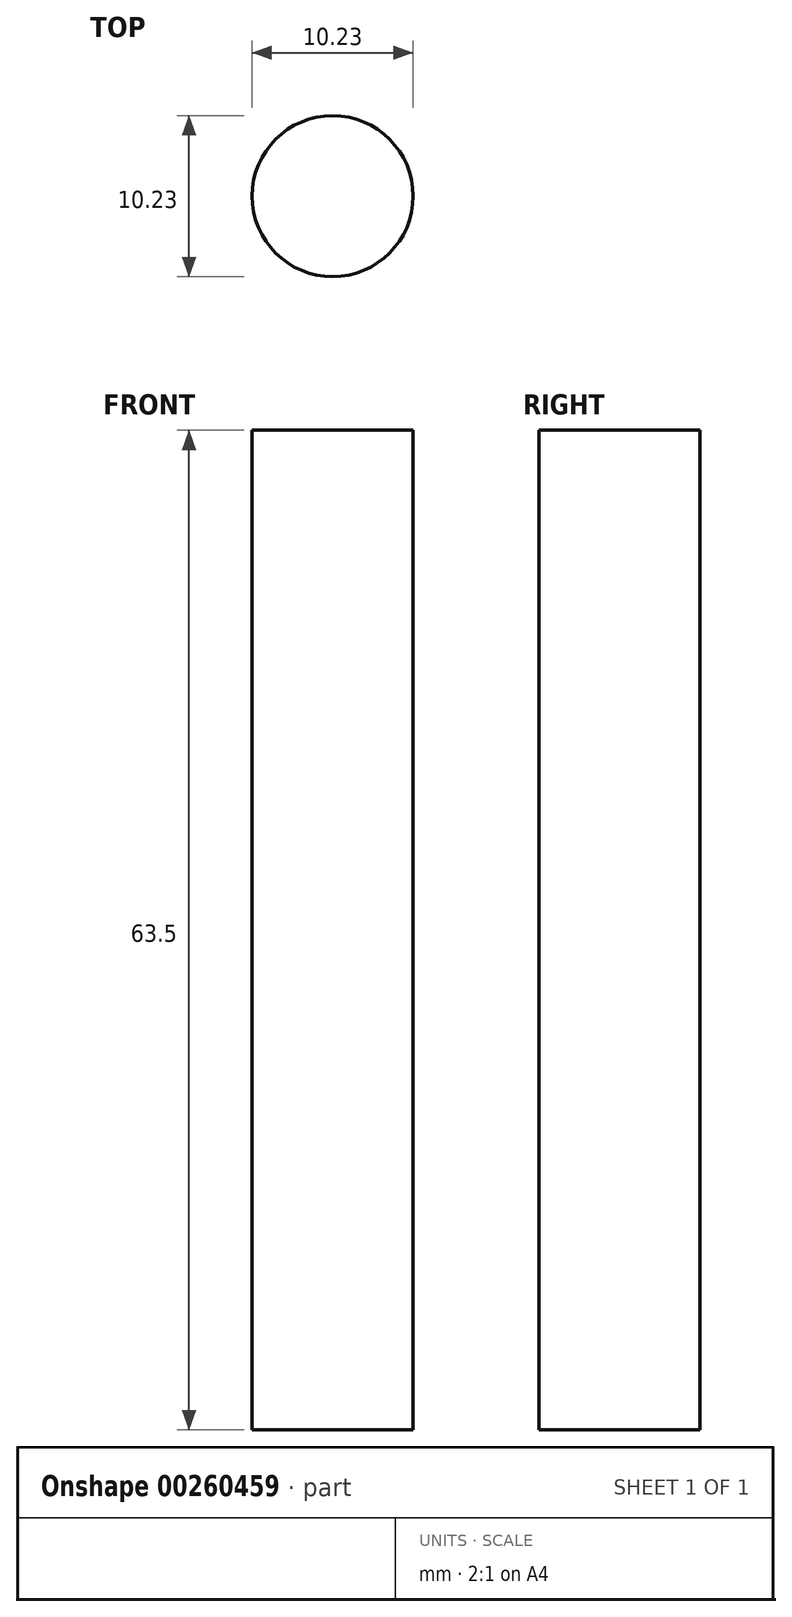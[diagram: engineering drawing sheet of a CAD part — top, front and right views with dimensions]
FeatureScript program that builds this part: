
annotation { "Feature Type Name" : "Feature", "Feature Type Description" : "" }
export const myFeature = defineFeature(function(context is Context, id is Id, definition is map)
    precondition{}
    {
        {
            var Q0;
            Q0=qCreatedBy(makeId("Top.planeOp"),FACE);
            var sketch = newSketch(context, id + "F0", { "sketchPlane" : qUnion([Q0])});
            skCircle(sketch, "E0", {"center": v(-37.8, 14.2) * mm, "radius": 5.11 * mm});
            skSolve(sketch);
        }
        {
            var Q0;
            Q0 = qSketchRegion(id + "F0", true);
            extrude(context, id + "F1", {"entities" : qUnion([Q0]), "depth" : 63.5 * mm});
        }
    });
